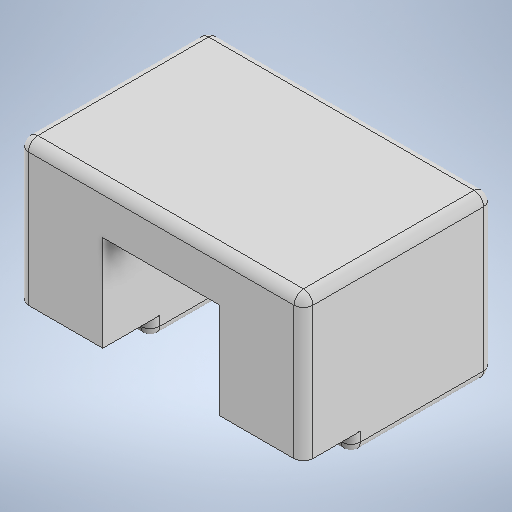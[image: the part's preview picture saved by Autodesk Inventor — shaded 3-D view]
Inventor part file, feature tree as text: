
AUTODESK INVENTOR PART (.ipt)
format: ipt  version: 2025 (Build 290162000, 162)  size: 362,496 bytes
history: native  units: in
note: dims shown in document units (in); Inventor stores cm internally (conversion verified against a paired STEP export)
features: projected_geometry x6, extrude x5, sketch x4, fillet x4, chamfer x2
ambient origin geometry x8: Origin, YZ Plane, XZ Plane, XY Plane, X Axis, Y Axis, Z Axis, Center Point
bodies: Solid1 (feature_tree)
feature tree (21):
  sketch  "Sketch1"  dims[d0=0.4843in d1=1.1811in]
  extrude  "Extrusion1"  Depth=1.1811in
  extrude  "Extrusion4"  Depth=0.5906in
  extrude  "Extrusion2"  Depth=0.1181in
  extrude  "Extrusion3"  Depth=0.1181in
  fillet  "Fillet1"  Radius=0.3937in
  extrude  "Extrusion5"  Depth=0.0394in
  chamfer  "Chamfer1"  Distance=0.5906in
  chamfer  "Chamfer2"  Distance=0.0394in
  fillet  "Fillet2"  Radius=0.0394in
  fillet  "Fillet3"  Radius=0.0945in
  fillet  "Fillet4"  Radius=0.0315in
  sketch  "Sketch2"  dims[d2=0.5906in d3=0.3976in]
  projected_geometry  "Projected Loop1"
  sketch  "Sketch3"  dims[d4=0.7874in d5=0.0in d6=0.1181in]
  projected_geometry  "Projected Loop2"
  projected_geometry  "Projected Loop3"
  projected_geometry  "Projected Loop4"
  projected_geometry  "Projected Loop5"
  sketch  "Sketch4"  dims[d7=0.3937in d8=0.0in d9=0.1181in d10=0.3937in d11=0.0in d12=0.0787in d13=0.5906in d14=0.0in d15=0.0394in d16=0.0394in d17=0.0945in d18=0.0315in d19=0.0787in d20=0.2362in d21=0.1181in d22=0.0in d23=0.0984in d24=0.125in d25=45.0deg d26=0.0394in d27=0.125in d28=45.0deg d29=0.0394in d30=0.0197in d31=0.0394in]
  projected_geometry  "Projected Loop6"
